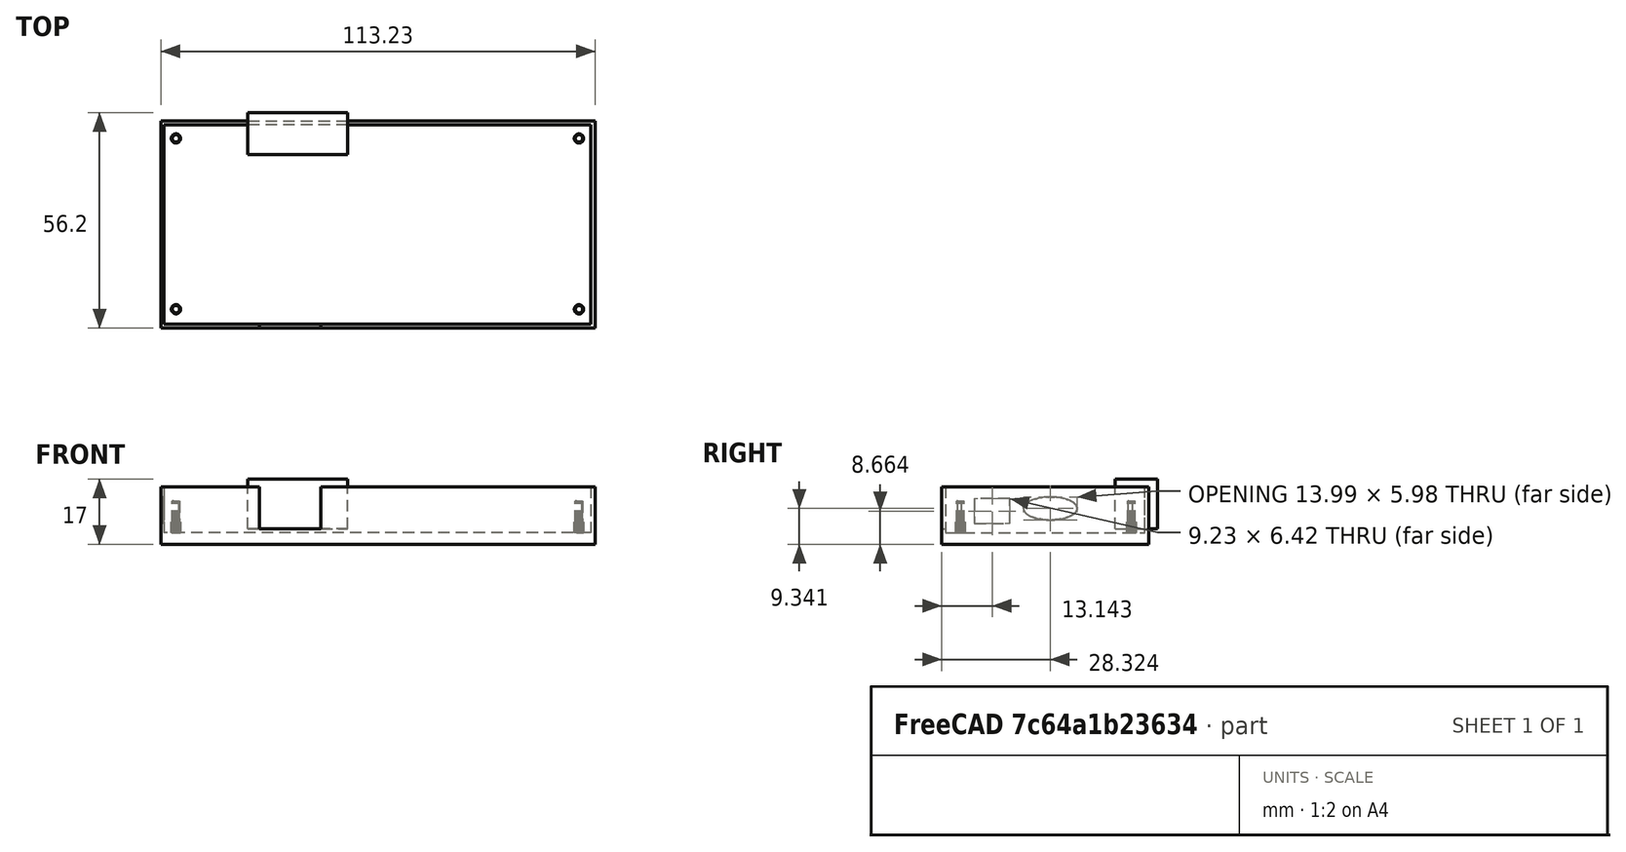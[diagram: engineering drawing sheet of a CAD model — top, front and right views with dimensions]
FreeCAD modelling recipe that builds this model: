
FCSTD DOCUMENT  (FreeCAD 1.0R39319 (Git))
Label: better_base
License: All rights reserved
LicenseURL: https://en.wikipedia.org/wiki/All_rights_reserved
objects: Part::Feature×2, Part::Box×2, Mesh::Feature×1, Part::Refine×1, PartDesign::FeatureBase×1, PartDesign::Boolean×1, PartDesign::Body×1, Part::Cut×1
note: 11 computed .brp shape members not serialized (recipe doc carries the construction recipe); baked Part::Feature solids carry a one-line shape summary decoded from their .brp

FEATURE [Mesh::Feature] Case_Body  label="Case-Body"
FEATURE [Part::Feature] Case_Body001
  shape: bbox 113.2 x 53.98 x 15 mm, 4772 faces, 0 solids (baked)
FEATURE [Part::Feature] Case_Body001_solid  label="Case_Body001 (Solid)"
  shape: bbox 113.2 x 53.98 x 15 mm, 4772 faces (baked)
FEATURE [Part::Refine] Case_Body001_solid001  label="Case_Body001 (Solid)001"
  Source = -> Case_Body001_solid
FEATURE [PartDesign::FeatureBase] BaseFeature
  BaseFeature = -> Case_Body001_solid001
  Suppressed = false
FEATURE [Part::Box] Box  label="Cube"
  AttacherType = Attacher::AttachEngine3D
  Height = 13
  Length = 26
  Placement = pos=(-29,20,4) rot=(0,0,1;0rad)
  Width = 11
FEATURE [PartDesign::Boolean] Boolean
  BaseFeature = -> BaseFeature
  Group = -> [Box]
  Refine = true
  Suppressed = false
  Type = 1
  UsePlacement = true
FEATURE [PartDesign::Body] Body
  AllowCompound = false
  BaseFeature = -> Case_Body001_solid001
  Group = -> [BaseFeature,Boolean]
  Origin = -> Origin
  Tip = -> Boolean
FEATURE [Part::Box] Box001  label="Cube001"
  AttacherType = Attacher::AttachEngine3D
  Height = 13
  Length = 16
  Placement = pos=(-26,-28,4) rot=(0,0,1;0rad)
  Width = 9
FEATURE [Part::Cut] Cut
  Base = -> Body
  Tool = -> Box001
